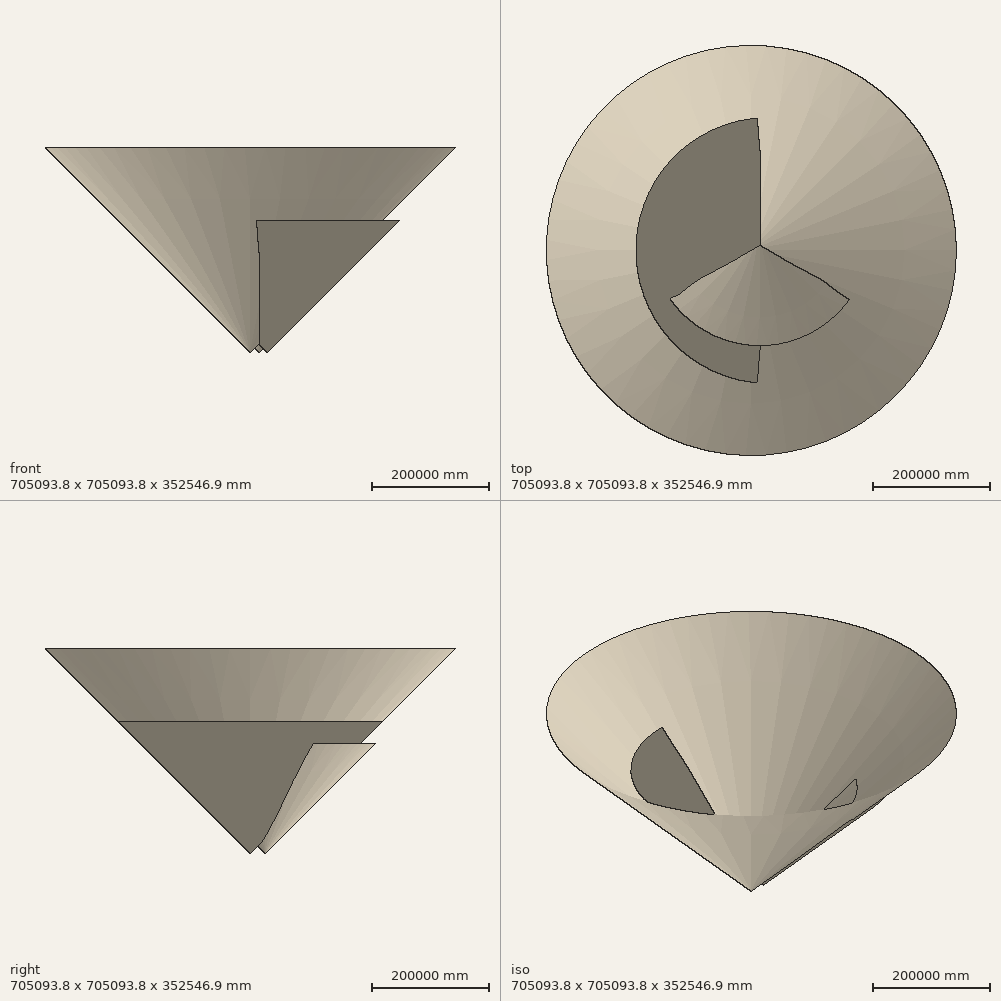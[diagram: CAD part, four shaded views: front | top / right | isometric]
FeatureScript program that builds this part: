
annotation { "Feature Type Name" : "Feature", "Feature Type Description" : "" }
export const myFeature = defineFeature(function(context is Context, id is Id, definition is map)
    precondition{}
    {
        {
            var Q0;
            Q0=qCreatedBy(makeId("Top.planeOp"),FACE);
            var sketch = newSketch(context, id + "F0", { "sketchPlane" : qUnion([Q0])});
            skLineSegment(sketch, "E0", {"start": v(0, 25980.76) * mm, "end": v(-15000, 0) * mm});
            skLineSegment(sketch, "E1", {"start": v(-15000, 0) * mm, "end": v(15000, 0) * mm});
            skLineSegment(sketch, "E2", {"start": v(15000, 0) * mm, "end": v(0, 25980.76) * mm});
            skSolve(sketch);
        }
        {
            var Q0;
            Q0=qCreatedBy(makeId("Front.planeOp"),FACE);
            var sketch = newSketch(context, id + "F1", { "sketchPlane" : qUnion([Q0])});
            skLineSegment(sketch, "E3", {"start": v(15000, 0) * mm, "end": v(-213510.02, 228510.02) * mm});
            skLineSegment(sketch, "E4", {"start": v(-213510.02, 228510.02) * mm, "end": v(15000, 0) * mm});
            skLineSegment(sketch, "E5", {"start": v(-15000, 0) * mm, "end": v(337546.9, 352546.9) * mm});
            skLineSegment(sketch, "E6", {"start": v(15000, 0) * mm, "end": v(15000, 17881.41) * mm, "construction": true});
            skLineSegment(sketch, "E7", {"start": v(-15000, 0) * mm, "end": v(-15000, 17319.98) * mm, "construction": true});
            skLineSegment(sketch, "E8", {"start": v(15000, 0) * mm, "end": v(-15000, 0) * mm});
            skSolve(sketch);
        }
        {
            var Q0;
            Q0=qCreatedBy(makeId("Right.planeOp"),FACE);
            var sketch = newSketch(context, id + "F2", { "sketchPlane" : qUnion([Q0])});
            skLineSegment(sketch, "E9.0", {"start": v(25980.76, 0) * mm, "end": v(0, 0) * mm});
            skLineSegment(sketch, "E10", {"start": v(25980.76, 0) * mm, "end": v(-163633.05, 189613.81) * mm});
            skLineSegment(sketch, "E11", {"start": v(25980.76, 0) * mm, "end": v(25980.76, 14322.42) * mm, "construction": true});
            skSolve(sketch);
        }
        {
            var Q0;
            Q0=sQuery(id+"F1.wireOp",EDGE,"E4");
            var Q1;
            Q1=sQuery(id+"F1.wireOp",EDGE,"E6");
            revolve(context, id + "F3", {"bodyType" : ToolBodyType.SURFACE, "surfaceOperationType" : NewSurfaceOperationType.NEW, "surfaceEntities" : qUnion([Q0]), "axis" : qUnion([Q1]), "revolveType" : RevolveType.FULL});
        }
        {
            var Q0;
            Q0=sQuery(id+"F1.wireOp",EDGE,"E5");
            var Q1;
            Q1=sQuery(id+"F1.wireOp",EDGE,"E7");
            revolve(context, id + "F4", {"bodyType" : ToolBodyType.SURFACE, "surfaceOperationType" : NewSurfaceOperationType.NEW, "surfaceEntities" : qUnion([Q0]), "axis" : qUnion([Q1]), "revolveType" : RevolveType.FULL});
        }
        {
            var Q0;
            Q0=sQuery(id+"F2.wireOp",EDGE,"E10");
            var Q1;
            Q1=sQuery(id+"F2.wireOp",EDGE,"E11");
            revolve(context, id + "F5", {"bodyType" : ToolBodyType.SURFACE, "surfaceOperationType" : NewSurfaceOperationType.NEW, "surfaceEntities" : qUnion([Q0]), "axis" : qUnion([Q1]), "revolveType" : RevolveType.FULL});
        }
    });
